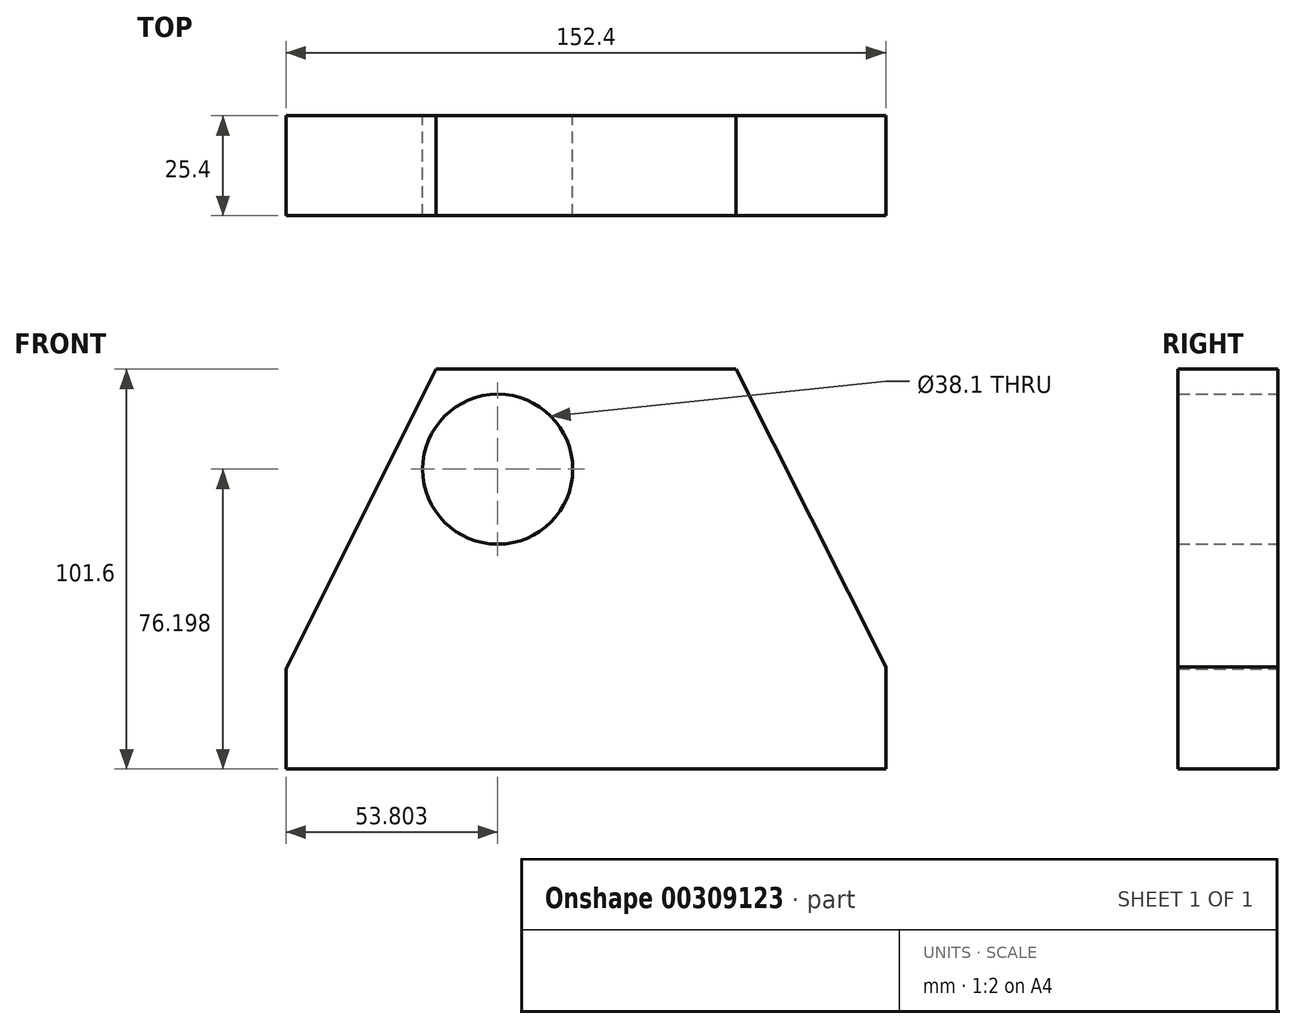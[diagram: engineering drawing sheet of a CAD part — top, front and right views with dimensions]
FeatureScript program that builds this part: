
annotation { "Feature Type Name" : "Feature", "Feature Type Description" : "" }
export const myFeature = defineFeature(function(context is Context, id is Id, definition is map)
    precondition{}
    {
        {
            var Q0;
            Q0=qCreatedBy(makeId("Front.planeOp"),FACE);
            var sketch = newSketch(context, id + "F0", { "sketchPlane" : qUnion([Q0])});
            skLineSegment(sketch, "E0", {"start": v(-94.88, -21.81) * mm, "end": v(-94.88, 3.59) * mm});
            skLineSegment(sketch, "E1", {"start": v(-94.88, 3.59) * mm, "end": v(-56.78, 79.79) * mm});
            skLineSegment(sketch, "E2", {"start": v(-56.78, 79.79) * mm, "end": v(19.42, 79.79) * mm});
            skLineSegment(sketch, "E3", {"start": v(57.52, -21.81) * mm, "end": v(57.52, 4.12) * mm});
            skLineSegment(sketch, "E4", {"start": v(57.52, 4.12) * mm, "end": v(19.42, 79.79) * mm});
            skLineSegment(sketch, "E5", {"start": v(-87.47, -21.81) * mm, "end": v(-94.88, -21.81) * mm});
            skLineSegment(sketch, "E6", {"start": v(-87.47, -21.81) * mm, "end": v(57.52, -21.81) * mm});
            skCircle(sketch, "E7", {"center": v(-41.08, 54.39) * mm, "radius": 19.05 * mm});
            skSolve(sketch);
        }
        {
            var Q0;
            Q0 = qSketchRegion(id + "F0", true);
            extrude(context, id + "F1", {"entities" : qUnion([Q0]), "depth" : 25.4 * mm});
        }
    });
